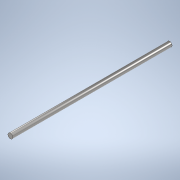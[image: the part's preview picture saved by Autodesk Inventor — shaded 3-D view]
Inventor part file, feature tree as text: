
AUTODESK INVENTOR PART (.ipt)
format: ipt  version: 2020 (Build 240168000, 168)  size: 93,696 bytes
history: native  units: mm
features: extrude x1, sketch x1
ambient origin geometry x8: Origin, YZ Plane, XZ Plane, XY Plane, X Axis, Y Axis, Z Axis, Center Point
bodies: Solid1 (feature_tree)
feature tree (2):
  extrude  "Extrusion1"  Depth=390.0mm TaperAngle=0.0deg
  sketch  "Sketch1"  dims[d0=12.0mm d1=390.0mm d2=0.0mm]
